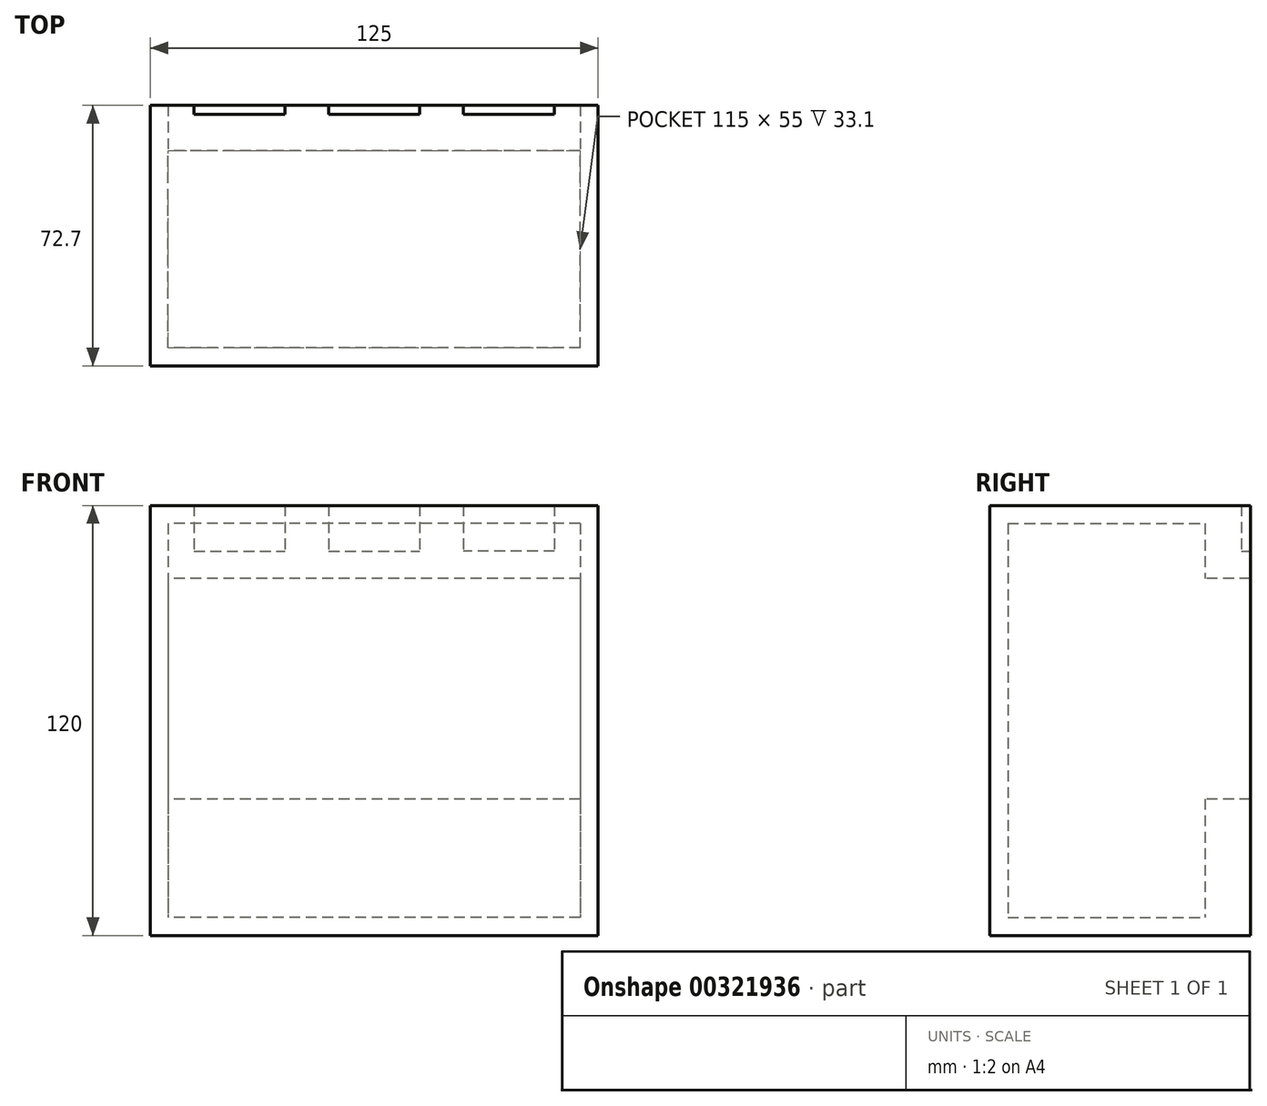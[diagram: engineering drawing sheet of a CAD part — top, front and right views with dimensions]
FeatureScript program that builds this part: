
annotation { "Feature Type Name" : "Feature", "Feature Type Description" : "" }
export const myFeature = defineFeature(function(context is Context, id is Id, definition is map)
    precondition{}
    {
        {
            var Q0;
            Q0=qCreatedBy(makeId("Front.planeOp"),FACE);
            var sketch = newSketch(context, id + "F0", { "sketchPlane" : qUnion([Q0])});
            skLineSegment(sketch, "E0.bottom", {"start": v(-62.5, -60) * mm, "end": v(62.5, -60) * mm});
            skLineSegment(sketch, "E0.top", {"start": v(-62.5, 60) * mm, "end": v(62.5, 60) * mm});
            skLineSegment(sketch, "E0.left", {"start": v(-62.5, -60) * mm, "end": v(-62.5, 60) * mm});
            skLineSegment(sketch, "E0.right", {"start": v(62.5, -60) * mm, "end": v(62.5, 60) * mm});
            skPoint(sketch, "E0.middle", {"position": v(0, 0) * mm});
            skSolve(sketch);
        }
        {
            var Q0;
            Q0 = qSketchRegion(id + "F0", true);
            extrude(context, id + "F1", {"entities" : qUnion([Q0]), "depth" : 60 * mm});
        }
        {
            var Q0;
            Q0=makeQuery(id+"F1.opExtrude","CAP_FACE",FACE,{"disambiguationData":[OSD([sQuery(id+"F0.wireOp",EDGE,"E0.bottom"),sQuery(id+"F0.wireOp",EDGE,"E0.top"),sQuery(id+"F0.wireOp",EDGE,"E0.left"),sQuery(id+"F0.wireOp",EDGE,"E0.right")])],"isStart":true});
            var sketch = newSketch(context, id + "F2", { "sketchPlane" : qUnion([Q0])});
            skLineSegment(sketch, "E1.bottom", {"start": v(-62.5, 60) * mm, "end": v(62.5, 60) * mm});
            skLineSegment(sketch, "E1.top", {"start": v(-62.5, 39.68) * mm, "end": v(62.5, 39.68) * mm});
            skLineSegment(sketch, "E1.left", {"start": v(-62.5, 60) * mm, "end": v(-62.5, 39.68) * mm});
            skLineSegment(sketch, "E1.right", {"start": v(62.5, 60) * mm, "end": v(62.5, 39.68) * mm});
            skLineSegment(sketch, "E2.bottom", {"start": v(-62.5, -21.9) * mm, "end": v(62.5, -21.9) * mm});
            skLineSegment(sketch, "E2.top", {"start": v(-62.5, -60) * mm, "end": v(62.5, -60) * mm});
            skLineSegment(sketch, "E2.left", {"start": v(-62.5, -21.9) * mm, "end": v(-62.5, -60) * mm});
            skLineSegment(sketch, "E2.right", {"start": v(62.5, -21.9) * mm, "end": v(62.5, -60) * mm});
            skSolve(sketch);
        }
        {
            var Q0;
            Q0 = qSketchRegion(id + "F2", true);
            extrude(context, id + "F3", {"entities" : qUnion([Q0]), "operationType" : NewBodyOperationType.ADD, "depth" : 12.7 * mm});
        }
        {
            var Q0;
            Q0=makeQuery(id+"F1.opExtrude","CAP_FACE",FACE,{"disambiguationData":[OSD([sQuery(id+"F0.wireOp",EDGE,"E0.bottom"),sQuery(id+"F0.wireOp",EDGE,"E0.top"),sQuery(id+"F0.wireOp",EDGE,"E0.left"),sQuery(id+"F0.wireOp",EDGE,"E0.right")])],"isStart":true});
            var sketch = newSketch(context, id + "F4", { "sketchPlane" : qUnion([Q0])});
            skLineSegment(sketch, "E3.bottom", {"start": v(-57.5, 55) * mm, "end": v(57.5, 55) * mm});
            skLineSegment(sketch, "E3.top", {"start": v(-57.5, -55) * mm, "end": v(57.5, -55) * mm});
            skLineSegment(sketch, "E3.left", {"start": v(-57.5, 55) * mm, "end": v(-57.5, -55) * mm});
            skLineSegment(sketch, "E3.right", {"start": v(57.5, 55) * mm, "end": v(57.5, -55) * mm});
            skPoint(sketch, "E3.middle", {"position": v(0, 0) * mm});
            skSolve(sketch);
        }
        {
            var Q0;
            Q0 = qSketchRegion(id + "F4", true);
            extrude(context, id + "F5", {"entities" : qUnion([Q0]), "operationType" : NewBodyOperationType.REMOVE, "oppositeDirection" : true, "depth" : 60 * mm - 5 * mm});
        }
        {
            var Q0;
            Q0=makeQuery(id+"F3.opExtrude","CAP_FACE",FACE,{"disambiguationData":[OSD([sQuery(id+"F2.wireOp",EDGE,"E1.bottom"),sQuery(id+"F2.wireOp",EDGE,"E1.top"),sQuery(id+"F2.wireOp",EDGE,"E1.left"),sQuery(id+"F2.wireOp",EDGE,"E1.right")])],"isStart":false});
            var sketch = newSketch(context, id + "F6", { "sketchPlane" : qUnion([Q0])});
            skLineSegment(sketch, "E4.bottom", {"start": v(-50.3, 60) * mm, "end": v(-24.9, 60) * mm});
            skLineSegment(sketch, "E4.top", {"start": v(-50.3, 47.3) * mm, "end": v(-24.9, 47.3) * mm});
            skLineSegment(sketch, "E4.left", {"start": v(-50.3, 60) * mm, "end": v(-50.3, 47.3) * mm});
            skLineSegment(sketch, "E4.right", {"start": v(-24.9, 60) * mm, "end": v(-24.9, 47.3) * mm});
            skLineSegment(sketch, "E5.bottom", {"start": v(0, 60) * mm, "end": v(-12.7, 60) * mm});
            skLineSegment(sketch, "E5.top", {"start": v(0, 47.3) * mm, "end": v(-12.7, 47.3) * mm});
            skLineSegment(sketch, "E5.right", {"start": v(-12.7, 60) * mm, "end": v(-12.7, 47.3) * mm});
            skLineSegment(sketch, "E6", {"start": v(0, 47.3) * mm, "end": v(0, 39.68) * mm, "construction": true});
            skLineSegment(sketch, "E7.MirrorCS", {"start": v(0, 47.3) * mm, "end": v(12.7, 47.3) * mm});
            skLineSegment(sketch, "E8.MirrorCS", {"start": v(12.7, 60) * mm, "end": v(12.7, 47.3) * mm});
            skLineSegment(sketch, "E9.MirrorCS", {"start": v(0, 60) * mm, "end": v(12.7, 60) * mm});
            skLineSegment(sketch, "E10.MirrorCS", {"start": v(24.9, 60) * mm, "end": v(24.9, 47.3) * mm});
            skLineSegment(sketch, "E11.MirrorCS", {"start": v(50.3, 47.3) * mm, "end": v(24.9, 47.3) * mm});
            skLineSegment(sketch, "E12.MirrorCS", {"start": v(50.3, 60) * mm, "end": v(50.3, 47.3) * mm});
            skLineSegment(sketch, "E13.MirrorCS", {"start": v(50.3, 60) * mm, "end": v(24.9, 60) * mm});
            skSolve(sketch);
        }
        {
            var Q0;
            Q0 = qSketchRegion(id + "F6", true);
            extrude(context, id + "F7", {"entities" : qUnion([Q0]), "operationType" : NewBodyOperationType.REMOVE, "oppositeDirection" : true, "depth" : 2.54 * mm});
        }
        {
            var Q0;
            {var subQ0=sQuery(id+"F0.wireOp",EDGE,"E0.left");Q0=makeQuery(id+"F5.boolean.opBoolean","SPLIT",FACE,{"disambiguationData":[TD([makeQuery(id+"F1.opExtrude","SWEPT_FACE",FACE,{"disambiguationData":[OSD([subQ0])]})])],"derivedFrom":makeQuery(id+"F1.opExtrude","CAP_FACE",FACE,{"disambiguationData":[OSD([sQuery(id+"F0.wireOp",EDGE,"E0.bottom"),sQuery(id+"F0.wireOp",EDGE,"E0.top"),subQ0,sQuery(id+"F0.wireOp",EDGE,"E0.right")])],"isStart":true})});}
            var sketch = newSketch(context, id + "F8", { "sketchPlane" : qUnion([Q0])});
            skLineSegment(sketch, "E14.bottom", {"start": v(57.5, 39.68) * mm, "end": v(62.5, 39.68) * mm});
            skLineSegment(sketch, "E14.top", {"start": v(57.5, -21.9) * mm, "end": v(62.5, -21.9) * mm});
            skLineSegment(sketch, "E14.left", {"start": v(57.5, 39.68) * mm, "end": v(57.5, -21.9) * mm});
            skLineSegment(sketch, "E14.right", {"start": v(62.5, 39.68) * mm, "end": v(62.5, -21.9) * mm});
            skLineSegment(sketch, "E15", {"start": v(0, 0) * mm, "end": v(0, 86.88) * mm, "construction": true});
            skLineSegment(sketch, "E16.MirrorCS", {"start": v(-57.5, 39.68) * mm, "end": v(-62.5, 39.68) * mm});
            skLineSegment(sketch, "E17.MirrorCS", {"start": v(-62.5, 39.68) * mm, "end": v(-62.5, -21.9) * mm});
            skLineSegment(sketch, "E18.MirrorCS", {"start": v(-57.5, 39.68) * mm, "end": v(-57.5, -21.9) * mm});
            skLineSegment(sketch, "E19.MirrorCS", {"start": v(-57.5, -21.9) * mm, "end": v(-62.5, -21.9) * mm});
            skSolve(sketch);
        }
        {
            var Q0;
            Q0 = qSketchRegion(id + "F8", true);
            extrude(context, id + "F9", {"entities" : qUnion([Q0]), "operationType" : NewBodyOperationType.ADD, "depth" : 12.7 * mm});
        }
    });
